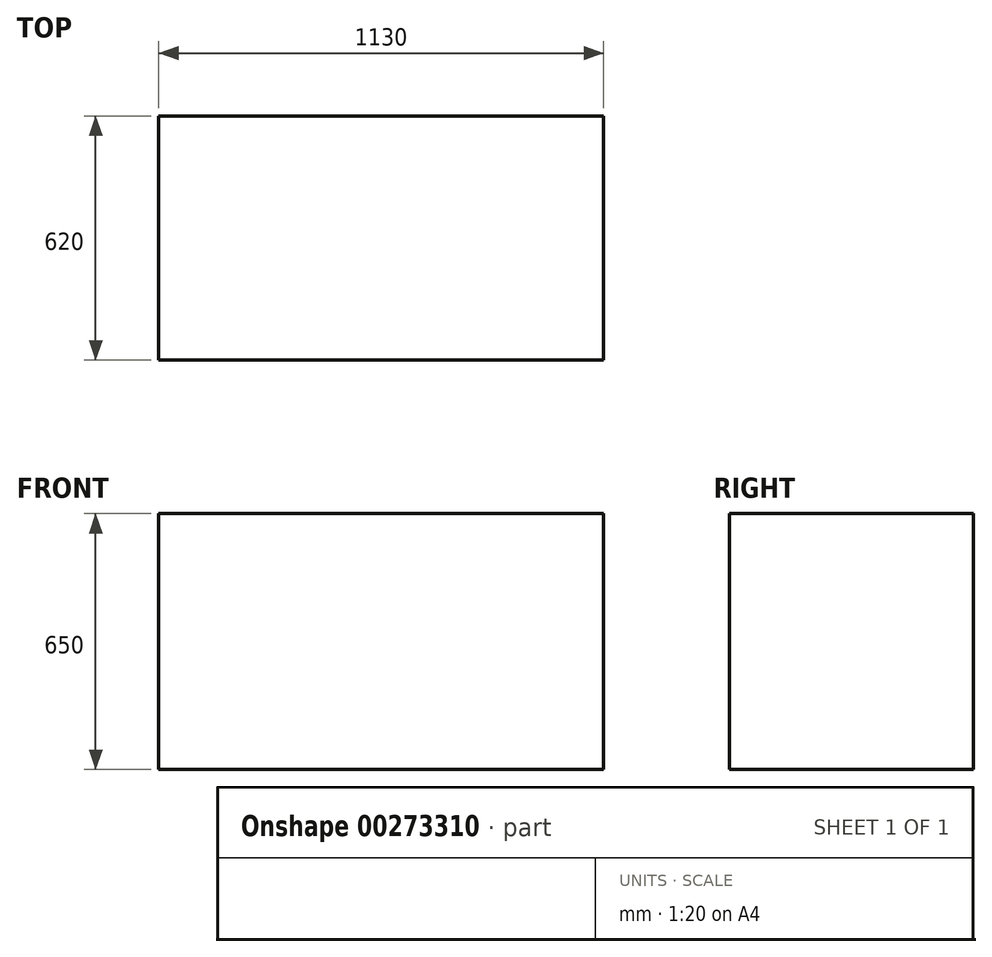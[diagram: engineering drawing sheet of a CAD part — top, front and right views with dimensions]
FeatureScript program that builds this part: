
annotation { "Feature Type Name" : "Feature", "Feature Type Description" : "" }
export const myFeature = defineFeature(function(context is Context, id is Id, definition is map)
    precondition{}
    {
        {
            var Q0;
            Q0=qCreatedBy(makeId("Top.planeOp"),FACE);
            var sketch = newSketch(context, id + "F0", { "sketchPlane" : qUnion([Q0])});
            skLineSegment(sketch, "E0.bottom", {"start": v(0, 0) * mm, "end": v(1130, 0) * mm});
            skLineSegment(sketch, "E0.top", {"start": v(0, 620) * mm, "end": v(1130, 620) * mm});
            skLineSegment(sketch, "E0.left", {"start": v(0, 0) * mm, "end": v(0, 620) * mm});
            skLineSegment(sketch, "E0.right", {"start": v(1130, 0) * mm, "end": v(1130, 620) * mm});
            skSolve(sketch);
        }
        {
            var Q0;
            Q0=makeQuery(id+"F0.imprint","IMPRINT",FACE,{"disambiguationData":[TD([[makeQuery(id+"F0.imprint","IMPRINT",EDGE,{"derivedFrom":sQuery(id+"F0.wireOp",EDGE,"E0.bottom")}),1.0]])]});
            extrude(context, id + "F1", {"entities" : qUnion([Q0]), "depth" : 650 * mm});
        }
    });
